# Revit family: Lochplatte VA
name_source: partatom
category: HLS-Bauteile
revit_build: Autodesk Revit 2017 (Build: 20190507_1515(x64)
units: mm (PartAtom-declared; Revit-internal decimal feet)

## family parameters
Arbeitsebenenbasiert = Ja
Beim Laden mit Abzugskörper schneiden = Nein
Bemaßung runder Anschluss = Durchmesser verwenden
Gemeinsam genutzt = Ja
Immer vertikal = Nein
Raumberechnungspunkt = Nein
Teiletyp = Normal

## types (2) — shared parameters
Anzugsmoment = 0.00 kN-m
B = 40 mm  [stored 0.131234 ft]
Breite = 40 mm  [stored 0.131234 ft]
Fabrikat = MEFA
Firma = MEFA Befestigungs- und Montagesysteme GmbH
Gewicht = 0.07 kg
Gewicht pro Bauteil = 0.07 kg
Kurztext2 = Bohrung 13 mm 45x40x5 mm
L = 45 mm  [stored 0.147638 ft]
Länge = 45 mm  [stored 0.147638 ft]
Material = Edelstahl
Mengeneinheit = St
Profiltyp = 45
S = 5 mm  [stored 0.0164042 ft]
Vorgabe-Ansicht = 1219 mm
d2 = 7 mm  [stored 0.0229659 ft]
vpe = 1 St
zero-valued in all types: Stärke Material

## per-type parameters (varying)
| type | Artikelnummer | EAN | Kurztext1 |
| Lochplatte 13 V2A | 0480401 | 4250928412638 | Lochplatte C-Profil 45 V2A |
| Lochplatte 13 V4A | 0481401 | 4250928412959 | Lochplatte C-Profil 45 V4A |

note: [stored X ft] marks values corroborated as IEEE doubles in the binary element streams (Revit-internal decimal feet)
